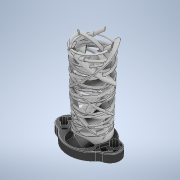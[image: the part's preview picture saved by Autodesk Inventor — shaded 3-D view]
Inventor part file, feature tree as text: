
AUTODESK INVENTOR PART (.ipt)
format: ipt  version: 2022 (Build 260153000, 153)  size: 7,145,472 bytes
history: native  units: mm
features: sketch x24, fillet x22, helix x12, extrude x10, other x2, revolve x2, imported_body x1
ambient origin geometry x8: Origin, YZ Plane, XZ Plane, XY Plane, X Axis, Y Axis, Z Axis, Center Point
bodies: Body1 (feature_tree), Body2 (feature_tree)
feature tree (73):
  imported_body  "Base"
  extrude  "Extrusion1"  Depth=70.0mm
  extrude  "Extrusion6"  Depth=70.0mm
  extrude  "Extrusion7"  Depth=72.0mm
  extrude  "Extrusion8"  Depth=3.0mm
  fillet  "Fillet5"  Radius=10.0mm
  extrude  "Extrusion9"  Depth=15.0mm
  extrude  "Extrusion10"  Depth=90.0mm
  fillet  "Fillet6"  Radius=20.0mm
  fillet  "Fillet10"  Radius=25.0mm
  fillet  "Fillet11"  Radius=30.0mm
  fillet  "Fillet12"  Radius=9.0mm
  fillet  "Fillet13"  Radius=60.0mm
  fillet  "Fillet14"  Radius=30.0mm
  extrude  "Extrusion11"  Depth=7.0mm
  extrude  "Extrusion12"  Depth=90.0mm
  other  "Work Axis1"
  revolve  "Revolution1"  [1 undecoded]
  extrude  "Extrusion13"  Depth=18.0mm
  helix  "Coil1"  [1 undecoded]
  helix  "Coil2"  [1 undecoded]
  helix  "Coil3"  [1 undecoded]
  helix  "Coil4"  [1 undecoded]
  helix  "Coil5"  [1 undecoded]
  helix  "Coil6"  [1 undecoded]
  helix  "Coil7"  [1 undecoded]
  helix  "Coil9"  [1 undecoded]
  helix  "Coil10"  [1 undecoded]
  helix  "Coil11"  [1 undecoded]
  helix  "Coil12"  [1 undecoded]
  helix  "Coil13"  [1 undecoded]
  extrude  "Extrusion14"  Depth=15.0mm
  fillet  "Fillet17"  Radius=75.0mm
  fillet  "Fillet18"  Radius=100.0mm
  fillet  "Fillet19"  Radius=30.0mm
  fillet  "Fillet20"  Radius=5.0mm
  fillet  "Fillet21"  Radius=2.0mm
  fillet  "Fillet22"  Radius=5.0mm
  fillet  "Fillet23"  Radius=5.0mm
  fillet  "Fillet24"  Radius=5.0mm
  fillet  "Fillet25"  [1 undecoded]
  fillet  "Fillet26"  Radius=2.5mm
  fillet  "Fillet27"  Radius=100.0mm
  fillet  "Fillet28"  Radius=2.5mm
  fillet  "Fillet29"  [1 undecoded]
  fillet  "Fillet30"  Radius=50.0mm
  fillet  "Fillet31"  Radius=3.0mm
  revolve  "Revolution2"  Angle=240.0deg
  sketch  "Sketch1"  dims[d4=28.0mm d5=0.0mm d79=70.0mm]
  sketch  "Sketch6"  dims[d80=80.0mm]
  sketch  "Sketch7"  dims[d87=24.0mm d88=25.0mm d89=22.5mm d90=26.0mm d91=18.0mm d92=18.0mm d94=9.0mm d95=21.5mm d96=21.5mm d97=10.75mm d98=10.75mm d99=25.0mm d100=70.0mm]
  sketch  "Sketch8"  dims[d101=70.0mm d102=72.0mm]
  sketch  "Sketch9"  dims[d103=72.0mm d104=3.0mm d105=10.0mm d106=0.0mm]
  sketch  "Sketch11"  dims[d107=100.0mm d108=15.0mm]
  sketch  "Sketch12"  dims[d109=25.0mm d110=0.0mm d111=90.0mm d112=20.0mm d113=25.0mm d114=0.0mm d115=30.0mm d116=9.0mm d117=60.0mm d118=30.0mm]
  sketch  "Sketch13"  dims[d119=62.0mm d120=7.0mm]
  other  "Tower"
  sketch  "Sketch14"  dims[d121=4.0mm d122=90.0mm]
  sketch  "Sketch15"  dims[d123=24.0mm d124=67.0mm]
  sketch  "Sketch16"  dims[d125=65.0mm d126=18.0mm d127=3.0mm d128=90.0mm d129=24.0mm d130=66.0mm d131=50.0mm d132=50.0mm d133=77.0mm d134=55.0mm d135=55.0mm d136=80.0mm d137=69.0mm d138=25.0mm d139=0.0mm]
  sketch  "Sketch17"  dims[d140=15.0mm d141=15.0mm d142=75.0mm d143=100.0mm d144=-0.349066mm d145=30.0mm d149=5.0mm d150=2.0mm d151=5.0mm d152=5.0mm d153=5.0mm d154=0.0mm d155=2.5mm d156=100.0mm d157=0.0mm d160=2.5mm d161=0.0mm d162=50.0mm d163=0.0mm d164=3.0mm]
  sketch  "Sketch18"  dims[d166=0.0mm d167=240.0deg]
  sketch  "Sketch19"  dims[d168=0.0mm]
  sketch  "Sketch20"  dims[d176=40.0mm d177=0.0mm]
  sketch  "Sketch21"  dims[d181=10.0mm]
  sketch  "Sketch22"  dims[d182=10.0mm]
  sketch  "Sketch23"  dims[d183=20.0mm]
  sketch  "Sketch24"  dims[d186=40.0mm]
  sketch  "Sketch25"  dims[d188=9.0mm]
  sketch  "Sketch26"  dims[d199=41.0mm d200=250.0mm d201=100.0mm d202=0.349066mm d203=90.0deg d204=90.0deg d205=0.0mm d206=0.0mm d207=5.0mm]
  sketch  "Sketch27"  dims[d208=7.0mm]
  sketch  "Sketch28"  dims[d209=43.0mm]
  sketch  "Sketch29"  dims[d210=14.0mm d211=9.0mm d220=277.0mm d221=260.0mm d222=13.5mm d223=0.244346mm d224=90.0deg d225=90.0deg d226=0.0mm d227=0.0mm d228=20.0mm d229=11.0mm d230=13.0mm d231=307.0mm d232=250.0mm d233=13.5mm d234=0.523599mm d235=90.0deg d236=90.0deg d237=0.0mm d238=0.0mm d239=25.0mm d240=13.0mm d241=14.5mm d242=313.0mm d243=250.0mm d244=13.5mm d245=0.523599mm d246=90.0deg d247=90.0deg d248=0.0mm d249=0.0mm d250=7.0mm d251=10.0mm d252=10.0mm d253=11.0mm d254=353.0mm d255=270.0mm d256=13.5mm d257=0.349066mm d258=90.0deg d259=90.0deg d260=0.0mm d261=0.0mm d262=8.0mm d263=5.0mm d264=8.0mm d265=40.0mm d266=317.0mm d267=270.0mm d268=13.5mm d269=0.698132mm d270=90.0deg d271=90.0deg d272=0.0mm d273=0.0mm d274=6.0mm d275=5.0mm d276=5.5mm d277=37.0mm d278=260.0mm d279=13.5mm d280=0.418879mm d281=90.0deg d282=90.0deg d283=0.0mm d284=0.0mm d285=9.0mm d286=4.5mm d287=48.0mm d312=71.0mm d313=240.0mm d314=13.5mm d315=0.303687mm d316=90.0deg d317=90.0deg d318=0.0mm d319=0.0mm d320=11.0mm d321=5.5mm d322=5.7mm d323=59.0mm d324=240.0mm d325=13.5mm d326=0.471239mm d327=90.0deg d328=90.0deg d329=0.0mm d330=0.0mm d331=6.0mm d332=3.2mm d333=8.0mm d334=3.8mm d335=271.0mm d336=260.0mm d337=13.5mm d338=0.401426mm d339=90.0deg d340=90.0deg d341=0.0mm d342=0.0mm d351=109.0mm d352=270.0mm d353=13.5mm d354=-0.122173mm d355=90.0deg d356=90.0deg d357=0.0mm d358=0.0mm d359=109.0mm d360=270.0mm d361=13.5mm d362=-0.122173mm d363=90.0deg d364=90.0deg d365=0.0mm d366=0.0mm d367=10.0mm d368=0.0mm d369=2.0mm d370=2.0mm d371=2.0mm d372=2.0mm d373=2.0mm d374=2.0mm d375=2.0mm d376=2.0mm d377=4.0mm d378=2.0mm d379=2.0mm d380=2.0mm d381=2.0mm d382=4.0mm d383=2.0mm d384=17.453293mm]
note: 15 required parameter values undecoded (feature->parameter linkage not recoverable at this tier; creation-order binding heuristic only, values carry confidence <= 0.55)